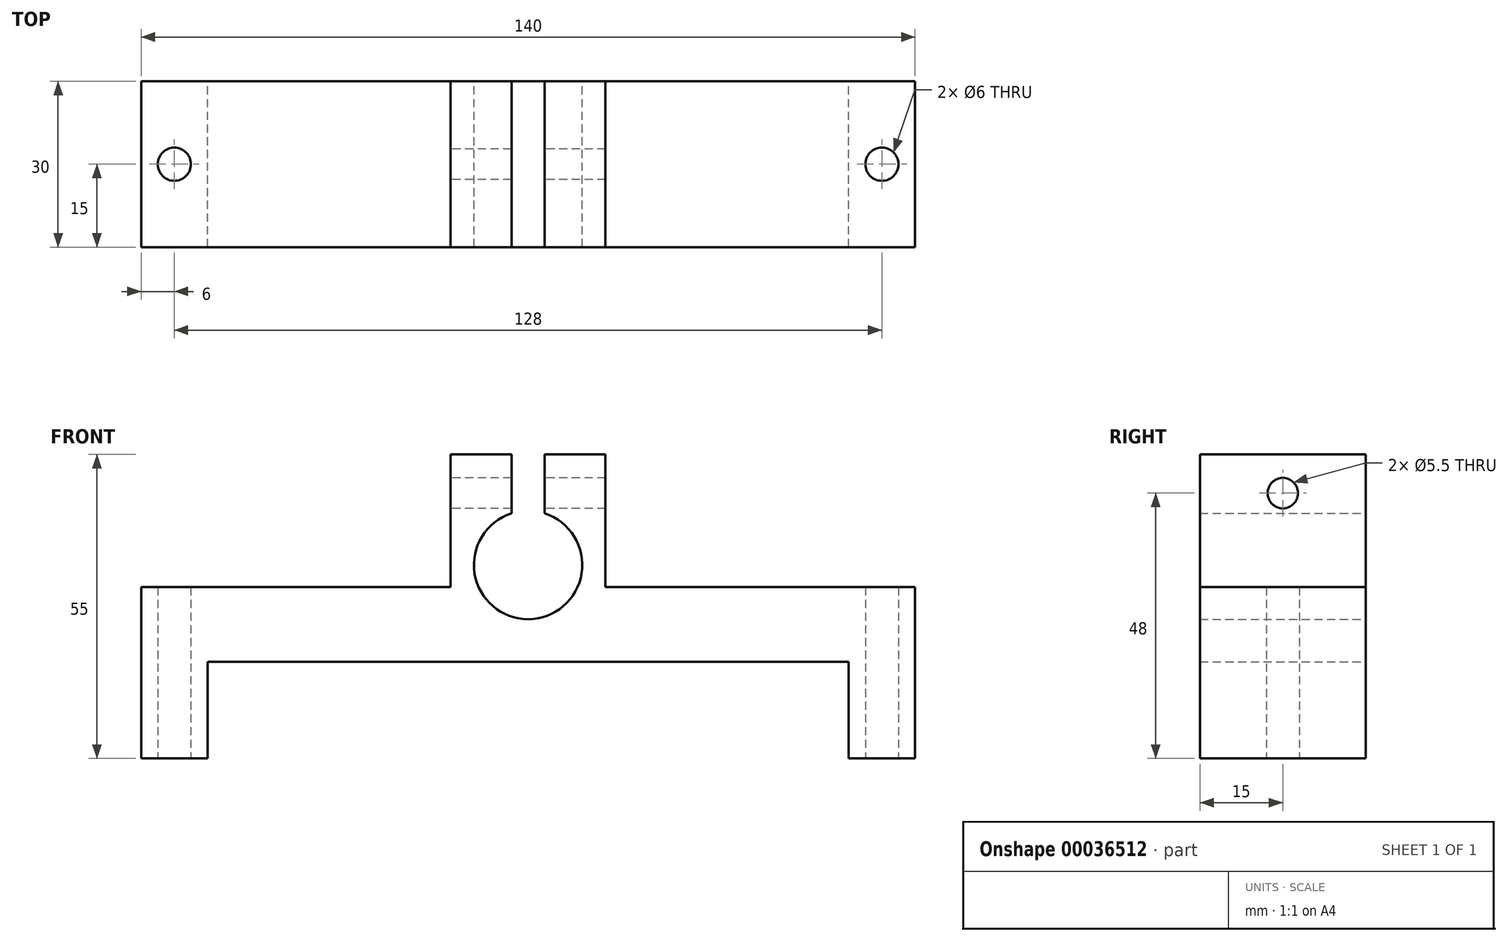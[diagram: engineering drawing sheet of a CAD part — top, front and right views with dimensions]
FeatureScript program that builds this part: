
annotation { "Feature Type Name" : "Feature", "Feature Type Description" : "" }
export const myFeature = defineFeature(function(context is Context, id is Id, definition is map)
    precondition{}
    {
        {
            var Q0;
            Q0=qCreatedBy(makeId("Top.planeOp"),FACE);
            var sketch = newSketch(context, id + "F0", { "sketchPlane" : qUnion([Q0])});
            skLineSegment(sketch, "E0.rect.bottom", {"start": v(70, -15) * mm, "end": v(-70, -15) * mm});
            skLineSegment(sketch, "E0.rect.top", {"start": v(70, 15) * mm, "end": v(-70, 15) * mm});
            skLineSegment(sketch, "E0.rect.left", {"start": v(70, -15) * mm, "end": v(70, 15) * mm});
            skLineSegment(sketch, "E0.rect.right", {"start": v(-70, -15) * mm, "end": v(-70, 15) * mm});
            skPoint(sketch, "E0.rect.middle", {"position": v(0, 0) * mm});
            skSolve(sketch);
        }
        {
            var Q0;
            Q0=makeQuery(id+"F0.imprint","IMPRINT",FACE,{"disambiguationData":[TD([[makeQuery(id+"F0.imprint","IMPRINT",EDGE,{"derivedFrom":sQuery(id+"F0.wireOp",EDGE,"E0.rect.bottom")}),-1.0]])]});
            extrude(context, id + "F1", {"entities" : qUnion([Q0]), "depth" : 55 * mm});
        }
        {
            var Q0;
            Q0=makeQuery(id+"F1.opExtrude","CAP_FACE",FACE,{"disambiguationData":[OSD([sQuery(id+"F0.wireOp",EDGE,"E0.rect.bottom"),sQuery(id+"F0.wireOp",EDGE,"E0.rect.top"),sQuery(id+"F0.wireOp",EDGE,"E0.rect.left"),sQuery(id+"F0.wireOp",EDGE,"E0.rect.right")])],"isStart":true});
            var sketch = newSketch(context, id + "F2", { "sketchPlane" : qUnion([Q0])});
            skLineSegment(sketch, "E1.bottom", {"start": v(-58, 15) * mm, "end": v(58, 15) * mm});
            skLineSegment(sketch, "E1.top", {"start": v(-58, -15) * mm, "end": v(58, -15) * mm});
            skLineSegment(sketch, "E1.left", {"start": v(-58, 15) * mm, "end": v(-58, -15) * mm});
            skLineSegment(sketch, "E1.right", {"start": v(58, 15) * mm, "end": v(58, -15) * mm});
            skSolve(sketch);
        }
        {
            var Q0;
            Q0=makeQuery(id+"F2.imprint","IMPRINT",FACE,{"disambiguationData":[TD([[makeQuery(id+"F2.imprint","IMPRINT",EDGE,{"derivedFrom":sQuery(id+"F2.wireOp",EDGE,"E1.bottom")}),1.0]])]});
            extrude(context, id + "F3", {"entities" : qUnion([Q0]), "operationType" : NewBodyOperationType.REMOVE, "oppositeDirection" : true, "depth" : 17.5 * mm});
        }
        {
            var Q0;
            Q0=makeQuery(id+"F1.opExtrude","SWEPT_FACE",FACE,{"disambiguationData":[OSD([sQuery(id+"F0.wireOp",EDGE,"E0.rect.bottom")])]});
            var sketch = newSketch(context, id + "F4", { "sketchPlane" : qUnion([Q0])});
            skPoint(sketch, "E2", {"position": v(0, 55) * mm});
            skPoint(sketch, "E3", {"position": v(0, 35) * mm});
            skSolve(sketch);
        }
        {
            var Q0;
            Q0=sQuery(id+"F4.wireOp",VERTEX,"E3");
            var Q1;
            Q1=makeQuery(id+"F1.opExtrude","SWEPT_BODY",BODY,{"disambiguationData":[OSD([sQuery(id+"F0.wireOp",EDGE,"E0.rect.bottom"),sQuery(id+"F0.wireOp",EDGE,"E0.rect.top"),sQuery(id+"F0.wireOp",EDGE,"E0.rect.left"),sQuery(id+"F0.wireOp",EDGE,"E0.rect.right")])]});
            hole(context, id + "F5", {"style" : HoleStyle.SIMPLE, "holeDiameter" : 19.6 * mm, "endStyle" : HoleEndStyle.THROUGH, "locations" : qUnion([Q0]), "scope" : qUnion([Q1])});
        }
        {
            var Q0;
            Q0=makeQuery(id+"F1.opExtrude","CAP_FACE",FACE,{"disambiguationData":[OSD([sQuery(id+"F0.wireOp",EDGE,"E0.rect.bottom"),sQuery(id+"F0.wireOp",EDGE,"E0.rect.top"),sQuery(id+"F0.wireOp",EDGE,"E0.rect.left"),sQuery(id+"F0.wireOp",EDGE,"E0.rect.right")])],"isStart":false});
            var sketch = newSketch(context, id + "F6", { "sketchPlane" : qUnion([Q0])});
            skPoint(sketch, "E4", {"position": v(-70, 0) * mm});
            skPoint(sketch, "E5", {"position": v(-64, 0) * mm});
            skSolve(sketch);
        }
        {
            var Q0;
            Q0=sQuery(id+"F6.wireOp",VERTEX,"E5");
            var Q1;
            Q1=makeQuery(id+"F1.opExtrude","SWEPT_BODY",BODY,{"disambiguationData":[OSD([sQuery(id+"F0.wireOp",EDGE,"E0.rect.bottom"),sQuery(id+"F0.wireOp",EDGE,"E0.rect.top"),sQuery(id+"F0.wireOp",EDGE,"E0.rect.left"),sQuery(id+"F0.wireOp",EDGE,"E0.rect.right")])]});
            hole(context, id + "F7", {"style" : HoleStyle.SIMPLE, "holeDiameter" : 6 * mm, "endStyle" : HoleEndStyle.THROUGH, "locations" : qUnion([Q0]), "scope" : qUnion([Q1])});
        }
        {
            var Q0;
            Q0=makeQuery(id+"F1.opExtrude","CAP_FACE",FACE,{"disambiguationData":[OSD([sQuery(id+"F0.wireOp",EDGE,"E0.rect.bottom"),sQuery(id+"F0.wireOp",EDGE,"E0.rect.top"),sQuery(id+"F0.wireOp",EDGE,"E0.rect.left"),sQuery(id+"F0.wireOp",EDGE,"E0.rect.right")])],"isStart":false});
            var sketch = newSketch(context, id + "F8", { "sketchPlane" : qUnion([Q0])});
            skPoint(sketch, "E6", {"position": v(64, 0) * mm});
            skPoint(sketch, "E6.positionSnap0", {"position": v(70, 0) * mm});
            skSolve(sketch);
        }
        {
            var Q0;
            Q0=sQuery(id+"F8.wireOp",VERTEX,"E6");
            var Q1;
            Q1=makeQuery(id+"F1.opExtrude","SWEPT_BODY",BODY,{"disambiguationData":[OSD([sQuery(id+"F0.wireOp",EDGE,"E0.rect.bottom"),sQuery(id+"F0.wireOp",EDGE,"E0.rect.top"),sQuery(id+"F0.wireOp",EDGE,"E0.rect.left"),sQuery(id+"F0.wireOp",EDGE,"E0.rect.right")])]});
            hole(context, id + "F9", {"style" : HoleStyle.SIMPLE, "holeDiameter" : 6 * mm, "endStyle" : HoleEndStyle.THROUGH, "locations" : qUnion([Q0]), "scope" : qUnion([Q1])});
        }
        {
            var Q0;
            Q0=makeQuery(id+"F1.opExtrude","CAP_FACE",FACE,{"disambiguationData":[OSD([sQuery(id+"F0.wireOp",EDGE,"E0.rect.bottom"),sQuery(id+"F0.wireOp",EDGE,"E0.rect.top"),sQuery(id+"F0.wireOp",EDGE,"E0.rect.left"),sQuery(id+"F0.wireOp",EDGE,"E0.rect.right")])],"isStart":false});
            var sketch = newSketch(context, id + "F10", { "sketchPlane" : qUnion([Q0])});
            skLineSegment(sketch, "E7.bottom", {"start": v(-70, 15) * mm, "end": v(-14, 15) * mm});
            skLineSegment(sketch, "E7.top", {"start": v(-70, -15) * mm, "end": v(-14, -15) * mm});
            skLineSegment(sketch, "E7.left", {"start": v(-70, 15) * mm, "end": v(-70, -15) * mm});
            skLineSegment(sketch, "E7.right", {"start": v(-14, 15) * mm, "end": v(-14, -15) * mm});
            skSolve(sketch);
        }
        {
            var Q0;
            Q0=makeQuery(id+"F10.imprint","IMPRINT",FACE,{"disambiguationData":[TD([[makeQuery(id+"F10.imprint","IMPRINT",EDGE,{"derivedFrom":sQuery(id+"F10.wireOp",EDGE,"E7.bottom")}),1.0]])]});
            extrude(context, id + "F11", {"entities" : qUnion([Q0]), "operationType" : NewBodyOperationType.REMOVE, "oppositeDirection" : true, "depth" : 24 * mm});
        }
        {
            var Q0;
            Q0=makeQuery(id+"F1.opExtrude","CAP_FACE",FACE,{"disambiguationData":[OSD([sQuery(id+"F0.wireOp",EDGE,"E0.rect.bottom"),sQuery(id+"F0.wireOp",EDGE,"E0.rect.top"),sQuery(id+"F0.wireOp",EDGE,"E0.rect.left"),sQuery(id+"F0.wireOp",EDGE,"E0.rect.right")])],"isStart":false});
            var sketch = newSketch(context, id + "F12", { "sketchPlane" : qUnion([Q0])});
            skLineSegment(sketch, "E8.bottom", {"start": v(14, 15) * mm, "end": v(70, 15) * mm});
            skLineSegment(sketch, "E8.top", {"start": v(14, -15) * mm, "end": v(70, -15) * mm});
            skLineSegment(sketch, "E8.left", {"start": v(14, 15) * mm, "end": v(14, -15) * mm});
            skLineSegment(sketch, "E8.right", {"start": v(70, 15) * mm, "end": v(70, -15) * mm});
            skSolve(sketch);
        }
        {
            var Q0;
            Q0=makeQuery(id+"F12.imprint","IMPRINT",FACE,{"disambiguationData":[TD([[makeQuery(id+"F12.imprint","IMPRINT",EDGE,{"derivedFrom":sQuery(id+"F12.wireOp",EDGE,"E8.bottom")}),1.0]])]});
            extrude(context, id + "F13", {"entities" : qUnion([Q0]), "operationType" : NewBodyOperationType.REMOVE, "oppositeDirection" : true, "depth" : 24 * mm});
        }
        {
            var Q0;
            Q0=makeQuery(id+"F13.boolean.opBoolean","COPY",FACE,{"derivedFrom":makeQuery(id+"F13.opExtrude","SWEPT_FACE",FACE,{"disambiguationData":[OSD([sQuery(id+"F12.wireOp",EDGE,"E8.left")])]})});
            var sketch = newSketch(context, id + "F14", { "sketchPlane" : qUnion([Q0])});
            skPoint(sketch, "E9", {"position": v(0, 48) * mm});
            skPoint(sketch, "E9.positionSnap0", {"position": v(0, 31) * mm});
            skSolve(sketch);
        }
        {
            var Q0;
            Q0=sQuery(id+"F14.wireOp",VERTEX,"E9");
            var Q1;
            Q1=makeQuery(id+"F1.opExtrude","SWEPT_BODY",BODY,{"disambiguationData":[OSD([sQuery(id+"F0.wireOp",EDGE,"E0.rect.bottom"),sQuery(id+"F0.wireOp",EDGE,"E0.rect.top"),sQuery(id+"F0.wireOp",EDGE,"E0.rect.left"),sQuery(id+"F0.wireOp",EDGE,"E0.rect.right")])]});
            hole(context, id + "F15", {"style" : HoleStyle.SIMPLE, "holeDiameter" : 5.5 * mm, "endStyle" : HoleEndStyle.THROUGH, "locations" : qUnion([Q0]), "scope" : qUnion([Q1])});
        }
        {
            var Q0;
            Q0=makeQuery(id+"F8.imprint","IMPRINT",FACE,{"disambiguationData":[TD([[makeQuery(id+"F8.imprint","IMPRINT",EDGE,{"derivedFrom":makeQuery(id+"F1.opExtrude","CAP_EDGE",EDGE,{"disambiguationData":[OSD([sQuery(id+"F0.wireOp",EDGE,"E0.rect.bottom")])],"isStart":false})}),-1.0]])]});
            var sketch = newSketch(context, id + "F16", { "sketchPlane" : qUnion([Q0])});
            skLineSegment(sketch, "E10.bottom", {"start": v(-3, 15.44) * mm, "end": v(3, 15.44) * mm});
            skLineSegment(sketch, "E10.top", {"start": v(-3, -15.01) * mm, "end": v(3, -15.01) * mm});
            skLineSegment(sketch, "E10.left", {"start": v(-3, 15.44) * mm, "end": v(-3, -15.01) * mm});
            skLineSegment(sketch, "E10.right", {"start": v(3, 15.44) * mm, "end": v(3, -15.01) * mm});
            skSolve(sketch);
        }
        {
            var Q0;
            Q0 = qSketchRegion(id + "F16", true);
            extrude(context, id + "F17", {"entities" : qUnion([Q0]), "operationType" : NewBodyOperationType.REMOVE, "oppositeDirection" : true, "depth" : 25 * mm});
        }
    });
